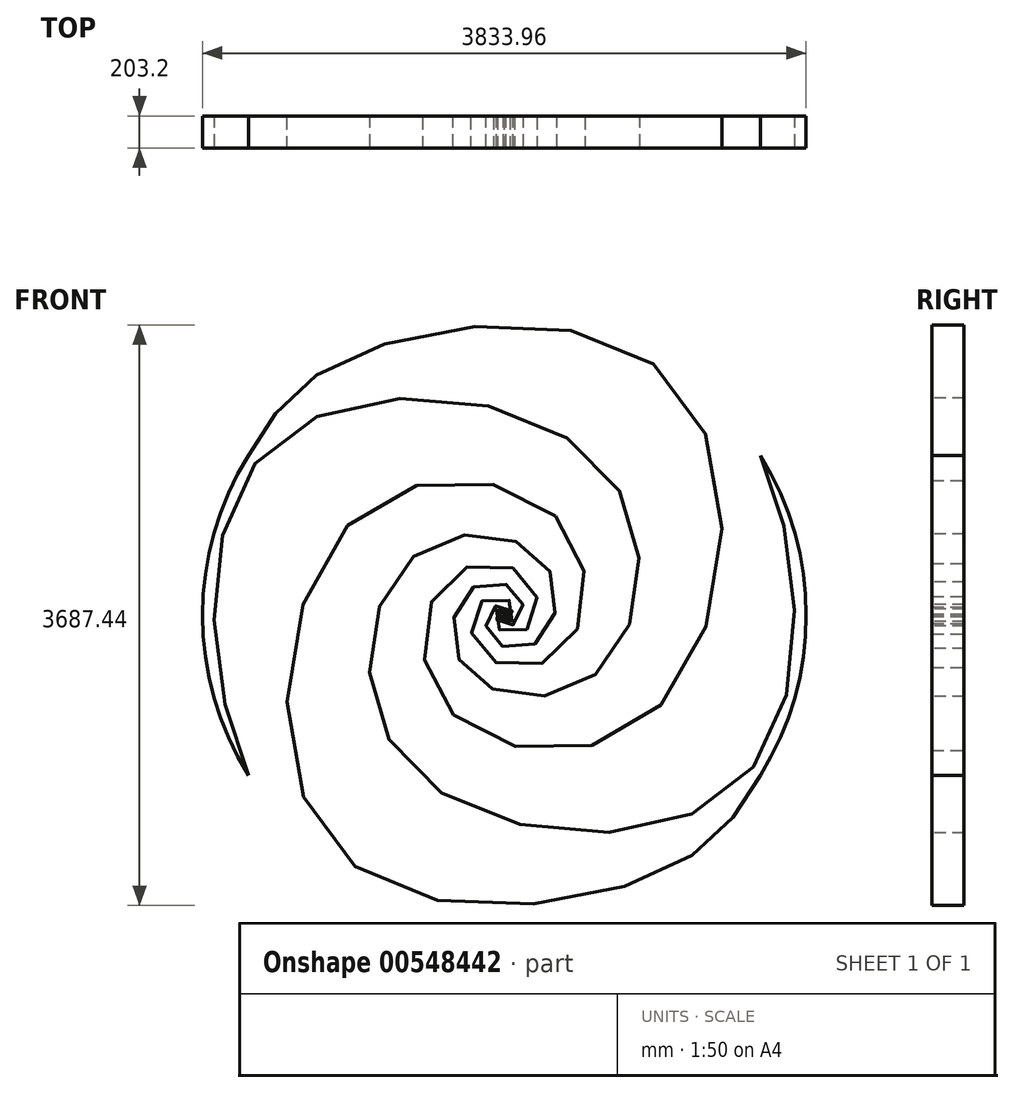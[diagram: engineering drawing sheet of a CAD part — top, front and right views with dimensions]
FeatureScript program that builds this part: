
annotation { "Feature Type Name" : "Feature", "Feature Type Description" : "" }
export const myFeature = defineFeature(function(context is Context, id is Id, definition is map)
    precondition{}
    {
        {
            var Q0;
            Q0=qCreatedBy(makeId("Front.planeOp"),FACE);
            var sketch = newSketch(context, id + "F0", { "sketchPlane" : qUnion([Q0])});
            skLineSegment(sketch, "E0", {"start": v(0, 0) * mm, "end": v(25.4, 0) * mm, "construction": true});
            skLineSegment(sketch, "E1", {"start": v(25.4, 0) * mm, "end": v(25.4, 25.4) * mm, "construction": true});
            skLineSegment(sketch, "E2", {"start": v(25.4, 25.4) * mm, "end": v(-25.4, 25.4) * mm, "construction": true});
            skLineSegment(sketch, "E3", {"start": v(-25.4, 25.4) * mm, "end": v(-25.4, -50.8) * mm, "construction": true});
            skLineSegment(sketch, "E4", {"start": v(-25.4, -50.8) * mm, "end": v(101.6, -50.8) * mm, "construction": true});
            skLineSegment(sketch, "E5", {"start": v(101.6, -50.8) * mm, "end": v(101.6, 152.4) * mm, "construction": true});
            skLineSegment(sketch, "E6", {"start": v(101.6, 152.4) * mm, "end": v(-228.6, 152.4) * mm, "construction": true});
            skLineSegment(sketch, "E7", {"start": v(-228.6, 152.4) * mm, "end": v(-228.6, -381) * mm, "construction": true});
            skLineSegment(sketch, "E8", {"start": v(-228.6, -381) * mm, "end": v(635, -381) * mm, "construction": true});
            skLineSegment(sketch, "E9", {"start": v(635, -381) * mm, "end": v(635, 1016) * mm, "construction": true});
            skLineSegment(sketch, "E10", {"start": v(635, 1016) * mm, "end": v(-1625.6, 1016) * mm, "construction": true});
            skLineSegment(sketch, "E11.1.0", {"start": v(0, 0) * mm, "end": v(0, 25.4) * mm, "construction": true});
            skLineSegment(sketch, "E11.1.1", {"start": v(0, 25.4) * mm, "end": v(-25.4, 25.4) * mm, "construction": true});
            skLineSegment(sketch, "E11.1.2", {"start": v(-25.4, 25.4) * mm, "end": v(-25.4, -25.4) * mm, "construction": true});
            skLineSegment(sketch, "E11.1.3", {"start": v(-25.4, -25.4) * mm, "end": v(50.8, -25.4) * mm, "construction": true});
            skLineSegment(sketch, "E11.1.4", {"start": v(50.8, -25.4) * mm, "end": v(50.8, 101.6) * mm, "construction": true});
            skLineSegment(sketch, "E11.1.5", {"start": v(50.8, 101.6) * mm, "end": v(-152.4, 101.6) * mm, "construction": true});
            skLineSegment(sketch, "E11.1.6", {"start": v(-152.4, 101.6) * mm, "end": v(-152.4, -228.6) * mm, "construction": true});
            skLineSegment(sketch, "E11.1.7", {"start": v(-152.4, -228.6) * mm, "end": v(381, -228.6) * mm, "construction": true});
            skLineSegment(sketch, "E11.1.8", {"start": v(381, -228.6) * mm, "end": v(381, 635) * mm, "construction": true});
            skLineSegment(sketch, "E11.1.9", {"start": v(381, 635) * mm, "end": v(-1016, 635) * mm, "construction": true});
            skLineSegment(sketch, "E11.1.10", {"start": v(-1016, 635) * mm, "end": v(-1016, -1625.6) * mm, "construction": true});
            skLineSegment(sketch, "E11.2.0", {"start": v(0, 0) * mm, "end": v(-25.4, 0) * mm, "construction": true});
            skLineSegment(sketch, "E11.2.1", {"start": v(-25.4, 0) * mm, "end": v(-25.4, -25.4) * mm, "construction": true});
            skLineSegment(sketch, "E11.2.2", {"start": v(-25.4, -25.4) * mm, "end": v(25.4, -25.4) * mm, "construction": true});
            skLineSegment(sketch, "E11.2.3", {"start": v(25.4, -25.4) * mm, "end": v(25.4, 50.8) * mm, "construction": true});
            skLineSegment(sketch, "E11.2.4", {"start": v(25.4, 50.8) * mm, "end": v(-101.6, 50.8) * mm, "construction": true});
            skLineSegment(sketch, "E11.2.5", {"start": v(-101.6, 50.8) * mm, "end": v(-101.6, -152.4) * mm, "construction": true});
            skLineSegment(sketch, "E11.2.6", {"start": v(-101.6, -152.4) * mm, "end": v(228.6, -152.4) * mm, "construction": true});
            skLineSegment(sketch, "E11.2.7", {"start": v(228.6, -152.4) * mm, "end": v(228.6, 381) * mm, "construction": true});
            skLineSegment(sketch, "E11.2.8", {"start": v(228.6, 381) * mm, "end": v(-635, 381) * mm, "construction": true});
            skLineSegment(sketch, "E11.2.9", {"start": v(-635, 381) * mm, "end": v(-635, -1016) * mm, "construction": true});
            skLineSegment(sketch, "E11.2.10", {"start": v(-635, -1016) * mm, "end": v(1625.6, -1016) * mm, "construction": true});
            skLineSegment(sketch, "E11.3.0", {"start": v(0, 0) * mm, "end": v(0, -25.4) * mm, "construction": true});
            skLineSegment(sketch, "E11.3.1", {"start": v(0, -25.4) * mm, "end": v(25.4, -25.4) * mm, "construction": true});
            skLineSegment(sketch, "E11.3.2", {"start": v(25.4, -25.4) * mm, "end": v(25.4, 25.4) * mm, "construction": true});
            skLineSegment(sketch, "E11.3.3", {"start": v(25.4, 25.4) * mm, "end": v(-50.8, 25.4) * mm, "construction": true});
            skLineSegment(sketch, "E11.3.4", {"start": v(-50.8, 25.4) * mm, "end": v(-50.8, -101.6) * mm, "construction": true});
            skLineSegment(sketch, "E11.3.5", {"start": v(-50.8, -101.6) * mm, "end": v(152.4, -101.6) * mm, "construction": true});
            skLineSegment(sketch, "E11.3.6", {"start": v(152.4, -101.6) * mm, "end": v(152.4, 228.6) * mm, "construction": true});
            skLineSegment(sketch, "E11.3.7", {"start": v(152.4, 228.6) * mm, "end": v(-381, 228.6) * mm, "construction": true});
            skLineSegment(sketch, "E11.3.8", {"start": v(-381, 228.6) * mm, "end": v(-381, -635) * mm, "construction": true});
            skLineSegment(sketch, "E11.3.9", {"start": v(-381, -635) * mm, "end": v(1016, -635) * mm, "construction": true});
            skLineSegment(sketch, "E11.3.10", {"start": v(1016, -635) * mm, "end": v(1016, 1625.6) * mm, "construction": true});
            skPoint(sketch, "E11.center", {"position": v(0, 0) * mm});
            skPoint(sketch, "E12.1.internal.snap0", {"position": v(50.8, 38.1) * mm});
            skSolve(sketch);
        }
        {
            var Q0;
            Q0=qCreatedBy(makeId("Front.planeOp"),FACE);
            var sketch = newSketch(context, id + "F1", { "sketchPlane" : qUnion([Q0])});
            skFitSpline(sketch, "E13", {"points": [v(0, 0) * mm, v(25.4, 0) * mm, v(25.4, 25.4) * mm, v(-25.4, 25.4) * mm, v(-25.4, -50.8) * mm, v(101.6, -50.8) * mm, v(101.6, 152.4) * mm, v(-228.6, 152.4) * mm, v(-228.6, -381) * mm, v(635, -381) * mm, v(635, 1016) * mm, v(-1625.6, 1016) * mm], "startDerivative": vector(916.81, -498.2) * mm, "endDerivative": vector(-7963.46, -7963.46) * mm});
            skFitSpline(sketch, "E14", {"points": [v(0, 0) * mm, v(-25.4, 0) * mm, v(-25.4, -25.4) * mm, v(25.4, -25.4) * mm, v(25.4, 50.8) * mm, v(-101.6, 50.8) * mm, v(-101.6, -152.4) * mm, v(228.6, -152.4) * mm, v(228.6, 381) * mm, v(-635, 381) * mm, v(-635, -1016) * mm, v(1625.6, -1016) * mm], "startDerivative": vector(-916.81, 498.2) * mm, "endDerivative": vector(7963.46, 7963.46) * mm});
            skSolve(sketch);
        }
        {
            var Q0;
            Q0=qCreatedBy(makeId("Front.planeOp"),FACE);
            var sketch = newSketch(context, id + "F2", { "sketchPlane" : qUnion([Q0])});
            skLineSegment(sketch, "E15", {"start": v(0, 0) * mm, "end": v(0, 25.4) * mm});
            skLineSegment(sketch, "E16", {"start": v(0, 25.4) * mm, "end": v(-25.4, 25.4) * mm});
            skLineSegment(sketch, "E17", {"start": v(-25.4, 25.4) * mm, "end": v(-25.4, -25.4) * mm});
            skLineSegment(sketch, "E18", {"start": v(-25.4, -25.4) * mm, "end": v(50.8, -25.4) * mm});
            skLineSegment(sketch, "E19", {"start": v(50.8, -25.4) * mm, "end": v(50.8, 101.6) * mm});
            skLineSegment(sketch, "E20", {"start": v(50.8, 101.6) * mm, "end": v(-152.4, 101.6) * mm});
            skLineSegment(sketch, "E21", {"start": v(-152.4, 101.6) * mm, "end": v(-152.4, -228.6) * mm});
            skLineSegment(sketch, "E22", {"start": v(-152.4, -228.6) * mm, "end": v(381, -228.6) * mm});
            skLineSegment(sketch, "E23", {"start": v(381, -228.6) * mm, "end": v(381, 635) * mm});
            skLineSegment(sketch, "E24", {"start": v(381, 635) * mm, "end": v(-1016, 635) * mm});
            skLineSegment(sketch, "E25", {"start": v(-1016, 635) * mm, "end": v(-1016, -1625.6) * mm});
            skLineSegment(sketch, "E26", {"start": v(0, 0) * mm, "end": v(25.4, 0) * mm, "construction": true});
            skLineSegment(sketch, "E27.1.0", {"start": v(228.6, -152.4) * mm, "end": v(228.6, 381) * mm});
            skLineSegment(sketch, "E27.1.1", {"start": v(-635, -1016) * mm, "end": v(1625.6, -1016) * mm});
            skLineSegment(sketch, "E27.1.2", {"start": v(-635, 381) * mm, "end": v(-635, -1016) * mm});
            skLineSegment(sketch, "E27.1.3", {"start": v(228.6, 381) * mm, "end": v(-635, 381) * mm});
            skLineSegment(sketch, "E27.1.4", {"start": v(-101.6, -152.4) * mm, "end": v(228.6, -152.4) * mm});
            skLineSegment(sketch, "E27.1.5", {"start": v(-101.6, 50.8) * mm, "end": v(-101.6, -152.4) * mm});
            skLineSegment(sketch, "E27.1.6", {"start": v(25.4, 50.8) * mm, "end": v(-101.6, 50.8) * mm});
            skLineSegment(sketch, "E27.1.7", {"start": v(0, 0) * mm, "end": v(0, 25.4) * mm, "construction": true});
            skLineSegment(sketch, "E27.1.8", {"start": v(25.4, -25.4) * mm, "end": v(25.4, 50.8) * mm});
            skLineSegment(sketch, "E27.1.9", {"start": v(-25.4, -25.4) * mm, "end": v(25.4, -25.4) * mm});
            skLineSegment(sketch, "E27.1.10", {"start": v(-25.4, 0) * mm, "end": v(-25.4, -25.4) * mm});
            skLineSegment(sketch, "E27.1.11", {"start": v(0, 0) * mm, "end": v(-25.4, 0) * mm});
            skPoint(sketch, "E27.center", {"position": v(0, 0) * mm});
            skLineSegment(sketch, "E28.3.2.0", {"start": v(1016, -635) * mm, "end": v(1016, 1625.6) * mm});
            skLineSegment(sketch, "E28.5.2.0", {"start": v(152.4, 228.6) * mm, "end": v(-381, 228.6) * mm});
            skLineSegment(sketch, "E28.6.2.0", {"start": v(-381, -635) * mm, "end": v(1016, -635) * mm});
            skLineSegment(sketch, "E28.9.2.0", {"start": v(-381, 228.6) * mm, "end": v(-381, -635) * mm});
            skLineSegment(sketch, "E28.12.2.0", {"start": v(152.4, -101.6) * mm, "end": v(152.4, 228.6) * mm});
            skLineSegment(sketch, "E28.15.2.0", {"start": v(-50.8, -101.6) * mm, "end": v(152.4, -101.6) * mm});
            skLineSegment(sketch, "E28.18.2.0", {"start": v(-50.8, 25.4) * mm, "end": v(-50.8, -101.6) * mm});
            skLineSegment(sketch, "E28.21.2.0", {"start": v(0, 0) * mm, "end": v(-25.4, 0) * mm, "construction": true});
            skLineSegment(sketch, "E28.24.2.0", {"start": v(25.4, 25.4) * mm, "end": v(-50.8, 25.4) * mm});
            skLineSegment(sketch, "E28.27.2.0", {"start": v(25.4, -25.4) * mm, "end": v(25.4, 25.4) * mm});
            skLineSegment(sketch, "E28.30.2.0", {"start": v(0, -25.4) * mm, "end": v(25.4, -25.4) * mm});
            skLineSegment(sketch, "E28.33.2.0", {"start": v(0, 0) * mm, "end": v(0, -25.4) * mm});
            skLineSegment(sketch, "E28.3.3.0", {"start": v(635, 1016) * mm, "end": v(-1625.6, 1016) * mm});
            skLineSegment(sketch, "E28.5.3.0", {"start": v(-228.6, 152.4) * mm, "end": v(-228.6, -381) * mm});
            skLineSegment(sketch, "E28.6.3.0", {"start": v(635, -381) * mm, "end": v(635, 1016) * mm});
            skLineSegment(sketch, "E28.9.3.0", {"start": v(-228.6, -381) * mm, "end": v(635, -381) * mm});
            skLineSegment(sketch, "E28.12.3.0", {"start": v(101.6, 152.4) * mm, "end": v(-228.6, 152.4) * mm});
            skLineSegment(sketch, "E28.15.3.0", {"start": v(101.6, -50.8) * mm, "end": v(101.6, 152.4) * mm});
            skLineSegment(sketch, "E28.18.3.0", {"start": v(-25.4, -50.8) * mm, "end": v(101.6, -50.8) * mm});
            skLineSegment(sketch, "E28.21.3.0", {"start": v(0, 0) * mm, "end": v(0, -25.4) * mm, "construction": true});
            skLineSegment(sketch, "E28.24.3.0", {"start": v(-25.4, 25.4) * mm, "end": v(-25.4, -50.8) * mm});
            skLineSegment(sketch, "E28.27.3.0", {"start": v(25.4, 25.4) * mm, "end": v(-25.4, 25.4) * mm});
            skLineSegment(sketch, "E28.30.3.0", {"start": v(25.4, 0) * mm, "end": v(25.4, 25.4) * mm});
            skLineSegment(sketch, "E28.33.3.0", {"start": v(0, 0) * mm, "end": v(25.4, 0) * mm});
            skLineSegment(sketch, "E29", {"start": v(-1625.6, 1016) * mm, "end": v(-1625.6, -1016) * mm, "construction": true});
            skLineSegment(sketch, "E30", {"start": v(1625.6, -1016) * mm, "end": v(1625.6, 1016) * mm, "construction": true});
            skSolve(sketch);
        }
        {
            var Q0;
            Q0=qCreatedBy(makeId("Front.planeOp"),FACE);
            var sketch = newSketch(context, id + "F3", { "sketchPlane" : qUnion([Q0])});
            skFitSpline(sketch, "E31", {"points": [v(0, 0) * mm, v(0, 25.4) * mm, v(-25.4, 25.4) * mm, v(-25.4, -25.4) * mm, v(50.8, -25.4) * mm, v(50.8, 101.6) * mm, v(-152.4, 101.6) * mm, v(-152.4, -228.6) * mm, v(381, -228.6) * mm, v(381, 635) * mm, v(-1016, 635) * mm, v(-1016, -1625.6) * mm], "startDerivative": vector(498.2, 916.81) * mm, "endDerivative": vector(7963.46, -7963.46) * mm});
            skFitSpline(sketch, "E32", {"points": [v(0, 0) * mm, v(0, -25.4) * mm, v(25.4, -25.4) * mm, v(25.4, 25.4) * mm, v(-50.8, 25.4) * mm, v(-50.8, -101.6) * mm, v(152.4, -101.6) * mm, v(152.4, 228.6) * mm, v(-381, 228.6) * mm, v(-381, -635) * mm, v(1016, -635) * mm, v(1016, 1625.6) * mm], "startDerivative": vector(-498.2, -916.81) * mm, "endDerivative": vector(-7963.46, 7963.46) * mm});
            skLineSegment(sketch, "E33", {"start": v(0, 7.44) * mm, "end": v(0, -7.44) * mm, "construction": true});
            skLineSegment(sketch, "E34", {"start": v(0, 7.44) * mm, "end": v(4.04, 7.44) * mm});
            skLineSegment(sketch, "E35", {"start": v(0, -7.44) * mm, "end": v(-4.04, -7.44) * mm});
            skSolve(sketch);
        }
        {
            var Q0;
            Q0=qCreatedBy(makeId("Front.planeOp"),FACE);
            var sketch = newSketch(context, id + "F4", { "sketchPlane" : qUnion([Q0])});
            skArc(sketch, "E36", {"start": v(1625.6, -1016) * mm, "mid": v(1867.9, 431.05) * mm, "end": v(1016, 1625.6) * mm});
            skSolve(sketch);
        }
        {
            var Q0;
            Q0=qCreatedBy(makeId("Front.planeOp"),FACE);
            var sketch = newSketch(context, id + "F5", { "sketchPlane" : qUnion([Q0])});
            skFitSpline(sketch, "E37.0", {"points": [v(0, 0) * mm, v(-4.04, -7.44) * mm, v(-6.81, -30.84) * mm, v(34.98, -33.65) * mm, v(40.57, 42.09) * mm, v(-77, 48.26) * mm, v(-88.87, -144.24) * mm, v(221.26, -162.66) * mm, v(251.54, 340.28) * mm, v(-561.62, 387.98) * mm, v(-639.09, -922.98) * mm, v(1482.22, -1075.79) * mm, v(1625.6, 1016) * mm, v(1016, 1625.6) * mm]});
            skFitSpline(sketch, "E37.1", {"points": [v(0, 0) * mm, v(-7.44, 4.04) * mm, v(-30.84, 6.81) * mm, v(-33.65, -34.98) * mm, v(42.09, -40.57) * mm, v(48.26, 77) * mm, v(-144.24, 88.87) * mm, v(-162.66, -221.26) * mm, v(340.28, -251.54) * mm, v(387.98, 561.62) * mm, v(-922.98, 639.09) * mm, v(-1075.79, -1482.22) * mm, v(1016, -1625.6) * mm, v(1625.6, -1016) * mm]});
            skArc(sketch, "E38.0", {"start": v(1625.6, -1016) * mm, "mid": v(1867.9, 431.05) * mm, "end": v(1016, 1625.6) * mm});
            skFitSpline(sketch, "E39.0", {"points": [v(0, 0) * mm, v(7.44, -4.04) * mm, v(30.84, -6.81) * mm, v(33.65, 34.98) * mm, v(-42.09, 40.57) * mm, v(-48.26, -77) * mm, v(144.24, -88.87) * mm, v(162.66, 221.26) * mm, v(-340.28, 251.54) * mm, v(-387.98, -561.62) * mm, v(922.98, -639.09) * mm, v(1075.79, 1482.22) * mm, v(-1016, 1625.6) * mm, v(-1625.6, 1016) * mm]});
            skSolve(sketch);
        }
        {
            var Q0;
            {var subQ0=sQuery(id+"F5.wireOp",EDGE,"E38.0");Q0=makeQuery(id+"F5.imprint","IMPRINT",FACE,{"disambiguationData":[TD([[makeQuery(id+"F5.imprint","IMPRINT",EDGE,{"derivedFrom":subQ0}),1.0]])]});}
            var Q1;
            {var subQ1=sQuery(id+"F5.wireOp",EDGE,"E37.1");var subQ2=sQuery(id+"F5.wireOp",EDGE,"E37.0");var subQ5=makeQuery(id+"F5.imprint","INTERSECT",VERTEX,{"disambiguationData":[OD(1.0)],"derivedFrom":[subQ2,subQ1]});Q1=makeQuery(id+"F5.imprint","IMPRINT",FACE,{"disambiguationData":[TD([[makeQuery(id+"F5.imprint","IMPRINT",EDGE,{"disambiguationData":[TD([[subQ5,-1.0]])],"derivedFrom":subQ2}),1.0]])]});}
            extrude(context, id + "F6", {"entities" : qUnion([Q0, Q1]), "depth" : 203.2 * mm, "offsetDistance" : 25.4 * mm});
        }
        {
            var Q0;
            Q0=makeQuery(id+"F6.opExtrude","SWEPT_BODY",BODY,{"disambiguationData":[OSD([sQuery(id+"F5.wireOp",EDGE,"E37.0"),sQuery(id+"F5.wireOp",EDGE,"E37.1"),sQuery(id+"F5.wireOp",EDGE,"E38.0")])]});
            var Q1;
            Q1=makeQuery(id+"F6.opExtrude","SWEPT_FACE",FACE,{"disambiguationData":[OSD([sQuery(id+"F5.wireOp",EDGE,"E38.0")])]});
            circularPattern(context, id + "F7", {"entities" : qUnion([Q0]), "axis" : qUnion([Q1]), "angle" : 360 * degree, "instanceCount" : 2, "equalSpace" : true});
        }
    });
